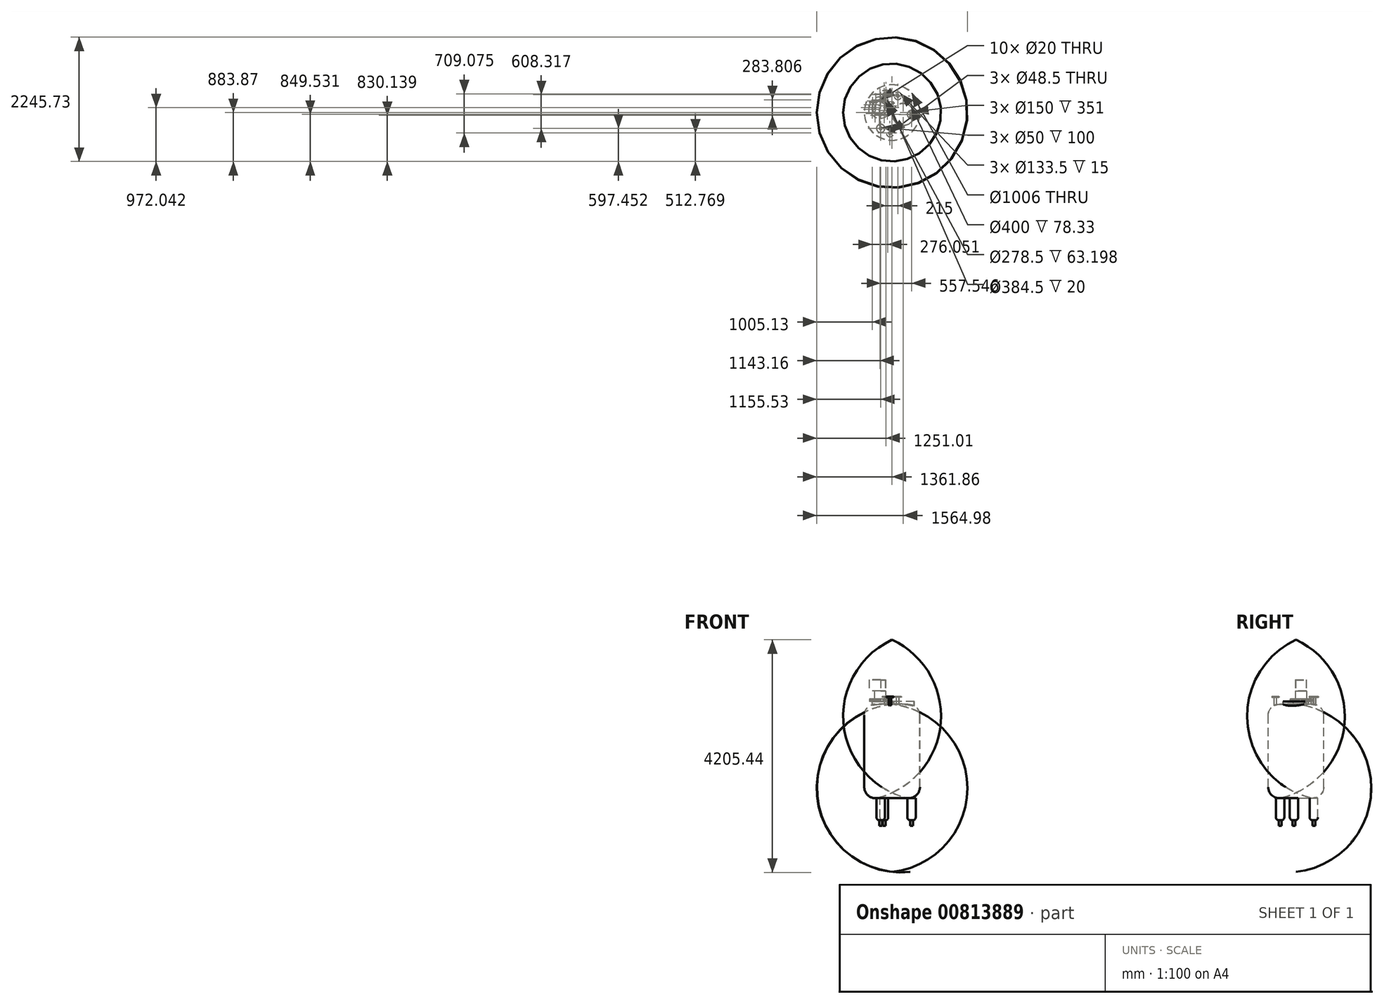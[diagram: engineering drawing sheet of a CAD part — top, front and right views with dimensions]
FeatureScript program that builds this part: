
annotation { "Feature Type Name" : "Feature", "Feature Type Description" : "" }
export const myFeature = defineFeature(function(context is Context, id is Id, definition is map)
    precondition{}
    {
        {
            var Q0;
            Q0=qCreatedBy(makeId("Front.planeOp"),FACE);
            var sketch = newSketch(context, id + "F0", { "sketchPlane" : qUnion([Q0])});
            skLineSegment(sketch, "E0", {"start": v(-503, 601.14) * mm, "end": v(-503, -697.32) * mm});
            skLineSegment(sketch, "E1", {"start": v(-3654, 0) * mm, "end": v(4045.38, 0) * mm, "construction": true});
            skArc(sketch, "E2.filletArc", {"start": v(-324.28, 800) * mm, "mid": v(-451.75, 734.82) * mm, "end": v(-503, 601.14) * mm});
            skPoint(sketch, "E3.visualSharp", {"position": v(-503, -2122.44) * mm});
            skArc(sketch, "E3.filletArc", {"start": v(-503, -697.32) * mm, "mid": v(-425.1, -855.72) * mm, "end": v(-252.07, -890.72) * mm});
            skLineSegment(sketch, "E4", {"start": v(0, 800) * mm, "end": v(0, -800) * mm});
            skArc(sketch, "E5", {"start": v(-252.07, -890.72) * mm, "mid": v(-124.04, -850.91) * mm, "end": v(0, -800) * mm});
            skArc(sketch, "E6", {"start": v(0, 800) * mm, "mid": v(-162.14, 808.65) * mm, "end": v(-324.28, 800) * mm});
            skArc(sketch, "E7.0", {"start": v(-252.84, -887.82) * mm, "mid": v(-124.4, -847.85) * mm, "end": v(0, -796.7) * mm});
            skArc(sketch, "E7.1", {"start": v(0, 796.98) * mm, "mid": v(-161.98, 805.65) * mm, "end": v(-323.96, 797.02) * mm});
            skArc(sketch, "E7.2", {"start": v(-323.96, 797.02) * mm, "mid": v(-449.52, 732.82) * mm, "end": v(-500, 601.14) * mm});
            skLineSegment(sketch, "E7.3", {"start": v(-500, 601.14) * mm, "end": v(-500, -697.32) * mm});
            skArc(sketch, "E7.4", {"start": v(-500, -697.32) * mm, "mid": v(-423.26, -853.35) * mm, "end": v(-252.84, -887.82) * mm});
            skLineSegment(sketch, "E8", {"start": v(0, 1704.23) * mm, "end": v(0, -2084.6) * mm, "construction": true});
            skSolve(sketch);
        }
        {
            var Q0;
            Q0=makeQuery(id+"F0.imprint","IMPRINT",FACE,{"disambiguationData":[TD([[makeQuery(id+"F0.imprint","IMPRINT",EDGE,{"derivedFrom":sQuery(id+"F0.wireOp",EDGE,"E0")}),1.0]])]});
            var Q1;
            Q1=sQuery(id+"F0.wireOp",EDGE,"E8");
            revolve(context, id + "F1", {"surfaceOperationType" : NewSurfaceOperationType.NEW, "entities" : qUnion([Q0]), "axis" : qUnion([Q1]), "revolveType" : RevolveType.FULL});
        }
        {
            var Q0;
            Q0=qCreatedBy(makeId("Top.planeOp"),FACE);
            cPlane(context, id + "F2", {"entities" : qUnion([Q0]), "cplaneType" : CPlaneType.OFFSET, "offset" : 850.9 * mm, "width" : 152.4 * mm, "height" : 152.4 * mm});
        }
        {
            var Q0;
            Q0=qCreatedBy(id+"F2.planeOp",FACE);
            var sketch = newSketch(context, id + "F3", { "sketchPlane" : qUnion([Q0])});
            skCircle(sketch, "E9", {"center": v(203.12, -34.34) * mm, "radius": 200 * mm});
            skCircle(sketch, "E10", {"center": v(203.12, -34.34) * mm, "radius": 197 * mm});
            skSolve(sketch);
        }
        {
            var Q0;
            Q0 = qSketchRegion(id + "F3", true);
            extrude(context, id + "F4", {"entities" : qUnion([Q0]), "operationType" : NewBodyOperationType.ADD, "endBound" : BoundingType.UP_TO_NEXT, "oppositeDirection" : true, "depth" : 25.4 * mm, "offsetDistance" : 25.4 * mm});
        }
        {
            var Q0;
            Q0=qCreatedBy(id+"F2.planeOp",FACE);
            var sketch = newSketch(context, id + "F5", { "sketchPlane" : qUnion([Q0])});
            skCircle(sketch, "E11", {"center": v(203.12, -34.34) * mm, "radius": 197 * mm});
            skSolve(sketch);
        }
        {
            var Q0;
            Q0 = qSketchRegion(id + "F5", true);
            extrude(context, id + "F6", {"entities" : qUnion([Q0]), "operationType" : NewBodyOperationType.REMOVE, "oppositeDirection" : true, "depth" : 243.84 * mm, "offsetDistance" : 25.4 * mm});
        }
        {
            var Q0;
            Q0=qCreatedBy(id+"F2.planeOp",FACE);
            var sketch = newSketch(context, id + "F7", { "sketchPlane" : qUnion([Q0])});
            skCircle(sketch, "E12", {"center": v(-218.7, 88.17) * mm, "radius": 139.25 * mm});
            skCircle(sketch, "E13", {"center": v(-218.7, 88.17) * mm, "radius": 136.25 * mm});
            skSolve(sketch);
        }
        {
            var Q0;
            Q0 = qSketchRegion(id + "F7", true);
            extrude(context, id + "F8", {"entities" : qUnion([Q0]), "operationType" : NewBodyOperationType.ADD, "endBound" : BoundingType.UP_TO_NEXT, "oppositeDirection" : true, "depth" : 25.4 * mm, "offsetDistance" : 25.4 * mm});
        }
        {
            var Q0;
            Q0=qCreatedBy(id+"F2.planeOp",FACE);
            var sketch = newSketch(context, id + "F9", { "sketchPlane" : qUnion([Q0])});
            skCircle(sketch, "E14", {"center": v(-218.7, 88.17) * mm, "radius": 136.25 * mm});
            skSolve(sketch);
        }
        {
            var Q0;
            Q0 = qSketchRegion(id + "F9", true);
            extrude(context, id + "F10", {"entities" : qUnion([Q0]), "operationType" : NewBodyOperationType.REMOVE, "oppositeDirection" : true, "depth" : 157.48 * mm, "offsetDistance" : 25.4 * mm});
        }
        {
            var Q0;
            Q0=makeQuery(id+"F8.opExtrude","CAP_FACE",FACE,{"disambiguationData":[OSD([sQuery(id+"F7.wireOp",EDGE,"E12"),sQuery(id+"F7.wireOp",EDGE,"E13")])],"isStart":true});
            var sketch = newSketch(context, id + "F11", { "sketchPlane" : qUnion([Q0])});
            skCircle(sketch, "E15", {"center": v(-218.7, 88.17) * mm, "radius": 192.25 * mm});
            skSolve(sketch);
        }
        {
            var Q0;
            Q0 = qSketchRegion(id + "F11", true);
            extrude(context, id + "F12", {"entities" : qUnion([Q0]), "operationType" : NewBodyOperationType.ADD, "depth" : 20 * mm, "offsetDistance" : 25.4 * mm});
        }
        {
            var Q0;
            Q0=qCreatedBy(id+"F2.planeOp",FACE);
            var sketch = newSketch(context, id + "F13", { "sketchPlane" : qUnion([Q0])});
            skCircle(sketch, "E16", {"center": v(-110.85, 337.97) * mm, "radius": 24.25 * mm});
            skCircle(sketch, "E17", {"center": v(-110.85, 337.97) * mm, "radius": 21.25 * mm});
            skCircle(sketch, "E18", {"center": v(104.15, 300.6) * mm, "radius": 24.25 * mm});
            skCircle(sketch, "E19", {"center": v(104.15, 300.6) * mm, "radius": 21.25 * mm});
            skCircle(sketch, "E20", {"center": v(-38.12, -371.1) * mm, "radius": 24.25 * mm});
            skCircle(sketch, "E21", {"center": v(-38.12, -371.1) * mm, "radius": 21.25 * mm});
            skSolve(sketch);
        }
        {
            var Q0;
            Q0 = qSketchRegion(id + "F13", true);
            extrude(context, id + "F14", {"entities" : qUnion([Q0]), "operationType" : NewBodyOperationType.ADD, "endBound" : BoundingType.UP_TO_NEXT, "oppositeDirection" : true, "depth" : 25.4 * mm, "offsetDistance" : 25.4 * mm, "hasSecondDirection" : true, "secondDirectionOppositeDirection" : false, "secondDirectionDepth" : 76.2 * mm});
        }
        {
            var Q0;
            Q0=qCreatedBy(id+"F2.planeOp",FACE);
            var sketch = newSketch(context, id + "F15", { "sketchPlane" : qUnion([Q0])});
            skCircle(sketch, "E22", {"center": v(-110.85, 337.97) * mm, "radius": 21.25 * mm});
            skSolve(sketch);
        }
        {
            var Q0;
            Q0 = qSketchRegion(id + "F15", true);
            extrude(context, id + "F16", {"entities" : qUnion([Q0]), "operationType" : NewBodyOperationType.REMOVE, "oppositeDirection" : true, "depth" : 203.2 * mm, "offsetDistance" : 25.4 * mm});
        }
        {
            var Q0;
            Q0=makeQuery(id+"F12.opExtrude","CAP_FACE",FACE,{"disambiguationData":[OSD([sQuery(id+"F11.wireOp",EDGE,"E15")])],"isStart":false});
            cPlane(context, id + "F17", {"entities" : qUnion([Q0]), "cplaneType" : CPlaneType.OFFSET, "offset" : 1 * mm, "width" : 152.4 * mm, "height" : 152.4 * mm});
        }
        {
            var Q0;
            Q0=qCreatedBy(id+"F17.planeOp",FACE);
            var sketch = newSketch(context, id + "F18", { "sketchPlane" : qUnion([Q0])});
            skCircle(sketch, "E23", {"center": v(-218.7, 88.17) * mm, "radius": 192.25 * mm});
            skSolve(sketch);
        }
        {
            var Q0;
            Q0 = qSketchRegion(id + "F18", true);
            extrude(context, id + "F19", {"entities" : qUnion([Q0]), "depth" : 20 * mm, "offsetDistance" : 25.4 * mm});
        }
        {
            var Q0;
            Q0=makeQuery(id+"F19.opExtrude","CAP_FACE",FACE,{"disambiguationData":[OSD([sQuery(id+"F18.wireOp",EDGE,"E23")])],"isStart":false});
            var sketch = newSketch(context, id + "F20", { "sketchPlane" : qUnion([Q0])});
            skCircle(sketch, "E24", {"center": v(-218.7, 88.17) * mm, "radius": 100 * mm});
            skSolve(sketch);
        }
        {
            var Q0;
            Q0 = qSketchRegion(id + "F20", true);
            extrude(context, id + "F21", {"entities" : qUnion([Q0]), "operationType" : NewBodyOperationType.ADD, "depth" : 150 * mm, "offsetDistance" : 25.4 * mm});
        }
        {
            var Q0;
            Q0=makeQuery(id+"F19.opExtrude","CAP_FACE",FACE,{"disambiguationData":[OSD([sQuery(id+"F18.wireOp",EDGE,"E23")])],"isStart":false});
            var sketch = newSketch(context, id + "F22", { "sketchPlane" : qUnion([Q0])});
            skCircle(sketch, "E25", {"center": v(-218.7, 88.17) * mm, "radius": 142.25 * mm, "construction": true});
            skCircle(sketch, "E26", {"center": v(-228.63, -53.73) * mm, "radius": 10 * mm});
            skCircle(sketch, "E27.1.0", {"center": v(-143.32, -32.47) * mm, "radius": 10 * mm});
            skCircle(sketch, "E27.2.0", {"center": v(-86.81, 34.88) * mm, "radius": 10 * mm});
            skCircle(sketch, "E27.3.0", {"center": v(-80.68, 122.58) * mm, "radius": 10 * mm});
            skCircle(sketch, "E27.4.0", {"center": v(-127.26, 197.14) * mm, "radius": 10 * mm});
            skCircle(sketch, "E27.5.0", {"center": v(-208.77, 230.07) * mm, "radius": 10 * mm});
            skCircle(sketch, "E27.6.0", {"center": v(-294.08, 208.8) * mm, "radius": 10 * mm});
            skCircle(sketch, "E27.7.0", {"center": v(-350.6, 141.46) * mm, "radius": 10 * mm});
            skCircle(sketch, "E27.8.0", {"center": v(-356.73, 53.76) * mm, "radius": 10 * mm});
            skCircle(sketch, "E27.9.0", {"center": v(-310.14, -20.8) * mm, "radius": 10 * mm});
            skSolve(sketch);
        }
        {
            var Q0;
            Q0 = qSketchRegion(id + "F22", true);
            var Q1;
            {var subQ0=sQuery(id+"F11.wireOp",EDGE,"E15");Q1=makeQuery(id+"F12.boolean.opBoolean","SPLIT",FACE,{"disambiguationData":[TD([makeQuery(id+"F8.opExtrude","SWEPT_FACE",FACE,{"disambiguationData":[OSD([sQuery(id+"F7.wireOp",EDGE,"E12")])]})])],"derivedFrom":makeQuery(id+"F12.opExtrude","CAP_FACE",FACE,{"disambiguationData":[OSD([subQ0])],"isStart":true})});}
            extrude(context, id + "F23", {"entities" : qUnion([Q0]), "operationType" : NewBodyOperationType.REMOVE, "oppositeDirection" : true, "depth" : 41.9 * mm, "endBoundEntityFace" : qUnion([Q1]), "offsetDistance" : 25.4 * mm});
        }
        {
            var Q0;
            Q0=makeQuery(id+"F21.opExtrude","CAP_FACE",FACE,{"disambiguationData":[OSD([sQuery(id+"F20.wireOp",EDGE,"E24")])],"isStart":false});
            var sketch = newSketch(context, id + "F24", { "sketchPlane" : qUnion([Q0])});
            skArc(sketch, "E28", {"start": v(-204.82, -10.86) * mm, "mid": v(-118.7, 88.17) * mm, "end": v(-204.82, 187.2) * mm});
            skLineSegment(sketch, "E29", {"start": v(-204.82, -10.86) * mm, "end": v(-418.7, -10.86) * mm});
            skLineSegment(sketch, "E30", {"start": v(-418.7, -10.86) * mm, "end": v(-418.7, 187.2) * mm});
            skLineSegment(sketch, "E31", {"start": v(-418.7, 187.2) * mm, "end": v(-204.82, 187.2) * mm});
            skSolve(sketch);
        }
        {
            var Q0;
            Q0 = qSketchRegion(id + "F24", true);
            extrude(context, id + "F25", {"entities" : qUnion([Q0]), "depth" : 200 * mm, "offsetDistance" : 25.4 * mm});
        }
        {
            var Q0;
            Q0=makeQuery(id+"F25.opExtrude","CAP_FACE",FACE,{"disambiguationData":[OSD([sQuery(id+"F24.wireOp",EDGE,"E28"),sQuery(id+"F24.wireOp",EDGE,"E29"),sQuery(id+"F24.wireOp",EDGE,"E30"),sQuery(id+"F24.wireOp",EDGE,"E31")])],"isStart":true});
            shell(context, id + "F26", {"entities" : qUnion([Q0]), "thickness" : 2.54 * mm});
        }
        {
            var Q0;
            {var subQ0=sQuery(id+"F11.wireOp",EDGE,"E15");Q0=makeQuery(id+"F12.boolean.opBoolean","SPLIT",FACE,{"disambiguationData":[TD([makeQuery(id+"F8.opExtrude","SWEPT_FACE",FACE,{"disambiguationData":[OSD([sQuery(id+"F7.wireOp",EDGE,"E12")])]})])],"derivedFrom":makeQuery(id+"F12.opExtrude","CAP_FACE",FACE,{"disambiguationData":[OSD([subQ0])],"isStart":true})});}
            cPlane(context, id + "F27", {"entities" : qUnion([Q0]), "cplaneType" : CPlaneType.OFFSET, "offset" : 1747.52 * mm, "width" : 152.4 * mm, "height" : 152.4 * mm});
        }
        {
            var Q0;
            Q0=qCreatedBy(id+"F27.planeOp",FACE);
            var sketch = newSketch(context, id + "F28", { "sketchPlane" : qUnion([Q0])});
            skCircle(sketch, "E32", {"center": v(0, 0) * mm, "radius": 353 * mm, "construction": true});
            skCircle(sketch, "E33", {"center": v(351.21, 35.48) * mm, "radius": 75 * mm});
            skCircle(sketch, "E34.1.0", {"center": v(-206.33, 286.42) * mm, "radius": 75 * mm});
            skCircle(sketch, "E34.2.0", {"center": v(-144.88, -321.9) * mm, "radius": 75 * mm});
            skSolve(sketch);
        }
        {
            var Q0;
            Q0 = qSketchRegion(id + "F28", true);
            var Q1;
            Q1=makeQuery(id+"F1.opRevolve","SWEPT_FACE",FACE,{"disambiguationData":[OSD([sQuery(id+"F0.wireOp",EDGE,"E3.filletArc")])]});
            extrude(context, id + "F29", {"entities" : qUnion([Q0]), "operationType" : NewBodyOperationType.ADD, "depth" : 400 * mm, "offsetDistance" : 25.4 * mm, "hasSecondDirection" : true, "secondDirectionOppositeDirection" : true, "secondDirectionDepth" : 1 * mm, "secondDirectionBoundEntityFace" : qUnion([Q1])});
        }
        {
            var Q0;
            Q0=makeQuery(id+"F29.opExtrude","CAP_FACE",FACE,{"disambiguationData":[OSD([sQuery(id+"F28.wireOp",EDGE,"E33")])],"isStart":false});
            var sketch = newSketch(context, id + "F30", { "sketchPlane" : qUnion([Q0])});
            skCircle(sketch, "E35", {"center": v(351.21, 35.48) * mm, "radius": 25 * mm});
            skSolve(sketch);
        }
        {
            var Q0;
            Q0 = qSketchRegion(id + "F30", true);
            extrude(context, id + "F31", {"entities" : qUnion([Q0]), "operationType" : NewBodyOperationType.ADD, "depth" : 100 * mm, "offsetDistance" : 25.4 * mm});
        }
        {
            var Q0;
            Q0=makeQuery(id+"F29.opExtrude","CAP_FACE",FACE,{"disambiguationData":[OSD([sQuery(id+"F28.wireOp",EDGE,"E34.2.0")])],"isStart":false});
            var sketch = newSketch(context, id + "F32", { "sketchPlane" : qUnion([Q0])});
            skCircle(sketch, "E36", {"center": v(-144.88, -321.9) * mm, "radius": 25 * mm});
            skSolve(sketch);
        }
        {
            var Q0;
            Q0 = qSketchRegion(id + "F32", true);
            extrude(context, id + "F33", {"entities" : qUnion([Q0]), "operationType" : NewBodyOperationType.ADD, "depth" : 100 * mm, "offsetDistance" : 25.4 * mm});
        }
        {
            var Q0;
            Q0=makeQuery(id+"F29.opExtrude","CAP_FACE",FACE,{"disambiguationData":[OSD([sQuery(id+"F28.wireOp",EDGE,"E34.1.0")])],"isStart":false});
            var sketch = newSketch(context, id + "F34", { "sketchPlane" : qUnion([Q0])});
            skCircle(sketch, "E37", {"center": v(-206.33, 286.42) * mm, "radius": 25 * mm});
            skSolve(sketch);
        }
        {
            var Q0;
            Q0 = qSketchRegion(id + "F34", true);
            extrude(context, id + "F35", {"entities" : qUnion([Q0]), "operationType" : NewBodyOperationType.ADD, "depth" : 100 * mm, "offsetDistance" : 25.4 * mm});
        }
        {
            var Q0;
            Q0=makeQuery(id+"F29.opExtrude","CAP_EDGE",EDGE,{"disambiguationData":[OSD([sQuery(id+"F28.wireOp",EDGE,"E34.2.0")])],"isStart":false});
            var Q1;
            Q1=makeQuery(id+"F29.opExtrude","CAP_EDGE",EDGE,{"disambiguationData":[OSD([sQuery(id+"F28.wireOp",EDGE,"E34.1.0")])],"isStart":false});
            var Q2;
            Q2=makeQuery(id+"F29.opExtrude","CAP_EDGE",EDGE,{"disambiguationData":[OSD([sQuery(id+"F28.wireOp",EDGE,"E33")])],"isStart":false});
            fillet(context, id + "F36", {"entities" : qUnion([Q0, Q1, Q2]), "radius" : 50 * mm, "tangentPropagation" : true, "allowEdgeOverflow" : false});
        }
        {
            var Q0;
            Q0=qCreatedBy(id+"F2.planeOp",FACE);
            var sketch = newSketch(context, id + "F37", { "sketchPlane" : qUnion([Q0])});
            skCircle(sketch, "E38", {"center": v(15.3, 171.3) * mm, "radius": 18.5 * mm});
            skCircle(sketch, "E39", {"center": v(15.3, 171.3) * mm, "radius": 15.5 * mm});
            skSolve(sketch);
        }
        {
            var Q0;
            Q0 = qSketchRegion(id + "F37", true);
            extrude(context, id + "F38", {"entities" : qUnion([Q0]), "operationType" : NewBodyOperationType.ADD, "endBound" : BoundingType.UP_TO_NEXT, "oppositeDirection" : true, "depth" : 25.4 * mm, "offsetDistance" : 25.4 * mm});
        }
        {
            var Q0;
            Q0=makeQuery(id+"F14.opExtrude","CAP_FACE",FACE,{"disambiguationData":[OSD([sQuery(id+"F13.wireOp",EDGE,"E18"),sQuery(id+"F13.wireOp",EDGE,"E19")])],"isStart":true});
            var sketch = newSketch(context, id + "F39", { "sketchPlane" : qUnion([Q0])});
            skCircle(sketch, "E40", {"center": v(104.15, 300.6) * mm, "radius": 21.25 * mm});
            skSolve(sketch);
        }
        {
            var Q0;
            Q0 = qSketchRegion(id + "F39", true);
            extrude(context, id + "F40", {"entities" : qUnion([Q0]), "operationType" : NewBodyOperationType.REMOVE, "oppositeDirection" : true, "depth" : 159.77 * mm, "offsetDistance" : 25.4 * mm});
        }
        {
            var Q0;
            Q0=makeQuery(id+"F38.opExtrude","CAP_FACE",FACE,{"disambiguationData":[OSD([sQuery(id+"F37.wireOp",EDGE,"E38"),sQuery(id+"F37.wireOp",EDGE,"E39")])],"isStart":true});
            var sketch = newSketch(context, id + "F41", { "sketchPlane" : qUnion([Q0])});
            skCircle(sketch, "E41", {"center": v(15.3, 171.3) * mm, "radius": 15.5 * mm});
            skSolve(sketch);
        }
        {
            var Q0;
            Q0 = qSketchRegion(id + "F41", true);
            extrude(context, id + "F42", {"entities" : qUnion([Q0]), "operationType" : NewBodyOperationType.REMOVE, "oppositeDirection" : true, "depth" : 53.34 * mm, "offsetDistance" : 25.4 * mm});
        }
        {
            var Q0;
            Q0=makeQuery(id+"F14.opExtrude","CAP_FACE",FACE,{"disambiguationData":[OSD([sQuery(id+"F13.wireOp",EDGE,"E20"),sQuery(id+"F13.wireOp",EDGE,"E21")])],"isStart":true});
            var sketch = newSketch(context, id + "F43", { "sketchPlane" : qUnion([Q0])});
            skCircle(sketch, "E42", {"center": v(-38.12, -371.1) * mm, "radius": 21.25 * mm});
            skSolve(sketch);
        }
        {
            var Q0;
            Q0 = qSketchRegion(id + "F43", true);
            extrude(context, id + "F44", {"entities" : qUnion([Q0]), "operationType" : NewBodyOperationType.REMOVE, "oppositeDirection" : true, "depth" : 142.5 * mm, "offsetDistance" : 25.4 * mm});
        }
        {
            var Q0;
            Q0=makeQuery(id+"F14.opExtrude","CAP_FACE",FACE,{"disambiguationData":[OSD([sQuery(id+"F13.wireOp",EDGE,"E20"),sQuery(id+"F13.wireOp",EDGE,"E21")])],"isStart":true});
            var sketch = newSketch(context, id + "F45", { "sketchPlane" : qUnion([Q0])});
            skCircle(sketch, "E43", {"center": v(-38.12, -371.1) * mm, "radius": 66.75 * mm});
            skSolve(sketch);
        }
        {
            var Q0;
            Q0 = qSketchRegion(id + "F45", true);
            extrude(context, id + "F46", {"entities" : qUnion([Q0]), "operationType" : NewBodyOperationType.ADD, "depth" : 15 * mm, "offsetDistance" : 25.4 * mm});
        }
        {
            var Q0;
            Q0=makeQuery(id+"F46.opExtrude","CAP_FACE",FACE,{"disambiguationData":[OSD([sQuery(id+"F45.wireOp",EDGE,"E43")])],"isStart":false});
            var sketch = newSketch(context, id + "F47", { "sketchPlane" : qUnion([Q0])});
            skCircle(sketch, "E44", {"center": v(-38.12, -371.1) * mm, "radius": 20 * mm});
            skSolve(sketch);
        }
        {
            var Q0;
            Q0 = qSketchRegion(id + "F47", true);
            extrude(context, id + "F48", {"entities" : qUnion([Q0]), "operationType" : NewBodyOperationType.REMOVE, "endBound" : BoundingType.UP_TO_NEXT, "oppositeDirection" : true, "depth" : 25.4 * mm, "offsetDistance" : 25.4 * mm});
        }
        {
            var Q0;
            Q0=makeQuery(id+"F14.opExtrude","CAP_FACE",FACE,{"disambiguationData":[OSD([sQuery(id+"F13.wireOp",EDGE,"E18"),sQuery(id+"F13.wireOp",EDGE,"E19")])],"isStart":true});
            var sketch = newSketch(context, id + "F49", { "sketchPlane" : qUnion([Q0])});
            skCircle(sketch, "E45", {"center": v(104.15, 300.6) * mm, "radius": 66.75 * mm});
            skSolve(sketch);
        }
        {
            var Q0;
            Q0 = qSketchRegion(id + "F49", true);
            extrude(context, id + "F50", {"entities" : qUnion([Q0]), "operationType" : NewBodyOperationType.ADD, "depth" : 15 * mm, "offsetDistance" : 25.4 * mm});
        }
        {
            var Q0;
            Q0=makeQuery(id+"F50.opExtrude","CAP_FACE",FACE,{"disambiguationData":[OSD([sQuery(id+"F49.wireOp",EDGE,"E45")])],"isStart":false});
            var sketch = newSketch(context, id + "F51", { "sketchPlane" : qUnion([Q0])});
            skCircle(sketch, "E46", {"center": v(104.15, 300.6) * mm, "radius": 19 * mm});
            skSolve(sketch);
        }
        {
            var Q0;
            Q0 = qSketchRegion(id + "F51", true);
            extrude(context, id + "F52", {"entities" : qUnion([Q0]), "operationType" : NewBodyOperationType.REMOVE, "endBound" : BoundingType.UP_TO_NEXT, "oppositeDirection" : true, "depth" : 25.4 * mm, "offsetDistance" : 25.4 * mm});
        }
        {
            var Q0;
            Q0=makeQuery(id+"F14.opExtrude","CAP_FACE",FACE,{"disambiguationData":[OSD([sQuery(id+"F13.wireOp",EDGE,"E16"),sQuery(id+"F13.wireOp",EDGE,"E17")])],"isStart":true});
            var sketch = newSketch(context, id + "F53", { "sketchPlane" : qUnion([Q0])});
            skCircle(sketch, "E47", {"center": v(-110.85, 337.97) * mm, "radius": 66.75 * mm});
            skSolve(sketch);
        }
        {
            var Q0;
            Q0 = qSketchRegion(id + "F53", true);
            extrude(context, id + "F54", {"entities" : qUnion([Q0]), "operationType" : NewBodyOperationType.ADD, "depth" : 15 * mm, "offsetDistance" : 25.4 * mm});
        }
        {
            var Q0;
            Q0=makeQuery(id+"F54.opExtrude","CAP_FACE",FACE,{"disambiguationData":[OSD([sQuery(id+"F53.wireOp",EDGE,"E47")])],"isStart":false});
            var sketch = newSketch(context, id + "F55", { "sketchPlane" : qUnion([Q0])});
            skCircle(sketch, "E48", {"center": v(-110.85, 337.97) * mm, "radius": 6.5 * mm});
            skSolve(sketch);
        }
        {
            var Q0;
            Q0 = qSketchRegion(id + "F55", true);
            extrude(context, id + "F56", {"entities" : qUnion([Q0]), "operationType" : NewBodyOperationType.REMOVE, "endBound" : BoundingType.UP_TO_NEXT, "oppositeDirection" : true, "depth" : 25.4 * mm, "offsetDistance" : 25.4 * mm});
        }
    });
